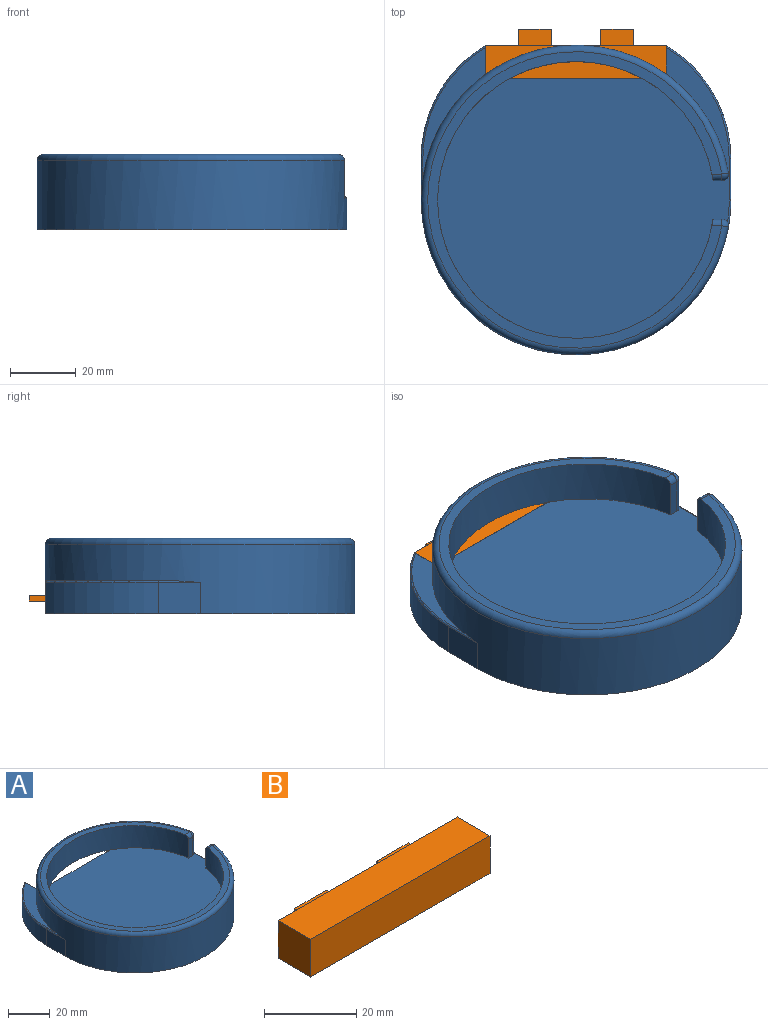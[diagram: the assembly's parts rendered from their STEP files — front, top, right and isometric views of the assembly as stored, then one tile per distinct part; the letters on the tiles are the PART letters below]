
ASSEMBLY  parts=2 mates=1
PART A: 30 faces, bbox 101.7x102.2x23.1 mm
  f0: cylinder r=42.17mm len=84.35mm, axis (0,0,-1), area 3289.9mm2, adj f5,f6,f8,f14,f15,f19,f22
  f1: plane 10x0.05mm, normal (1,0,0), area 0.5mm2, adj f4,f5,f10,f13
  f2: plane 39.64x19.18mm, normal (0,0,1), area 175.6mm2, adj f3,f9,f25,f26
  f3: cylinder r=47.18mm len=94.35mm, axis (0,0,-1), area 4558.3mm2, adj f2,f4,f5,f7,f8,f12,f16,f17
  f4: plane 94.35x94.25mm, normal (0,0,-1), area 6989.5mm2, adj f1,f3,f7,f9,f10,f11,f12,f13
  f5: plane 88.85x88.62mm, normal (0,0,1), area 5678.6mm2, adj f0,f1,f3,f10,f11,f13,f14,f15
  f6: plane 90.35x89.66mm, normal (0,0,1), area 775.7mm2, adj f0,f16,f19,f22
  f7: plane 12.62x9.5mm, normal (-1,0,0), area 119.9mm2, adj f3,f4,f24,f25
  f8: plane 55x10.15mm, normal (0,0,-1), area 261.9mm2, adj f0,f3,f9,f10,f11,f13
  f9: plane 10.12x10.12mm, normal (1,0,0), area 99.9mm2, adj f2,f4,f8,f10,f24,f26
  f10: plane 27.5x10mm, normal (0,1,0), area 275mm2, adj f1,f4,f5,f8,f9
  f11: plane 10.12x10.12mm, normal (-1,0,0), area 99.9mm2, adj f4,f5,f8,f13,f23,f29
  f12: plane 12.57x9.5mm, normal (1,0,0), area 119.4mm2, adj f3,f4,f23,f28
  f13: plane 27.5x10mm, normal (0,1,0), area 275mm2, adj f1,f4,f5,f8,f11
  f14: plane 11x2.72mm, normal (0,1,0), area 29.9mm2, adj f0,f5,f17,f19
  f15: plane 11x2.72mm, normal (0,-1,0), area 29.9mm2, adj f0,f5,f20,f22
  f16: torus R=45.17mm, axis (0,0,-1), area 865.7mm2, adj f3,f6,f18,f21
  f17: cylinder r=2mm len=11.5mm, axis (0,0,-1), area 38.8mm2, adj f3,f5,f14,f18,f27
  f18: sphere r=2mm, area 6.8mm2, adj f16,f17,f19
  f19: cylinder r=2mm len=3.05mm, axis (1,0,0), area 9.1mm2, adj f0,f6,f14,f18
  f20: cylinder r=2mm len=11mm, axis (0,0,-1), area 38.4mm2, adj f3,f5,f15,f21
  f21: sphere r=2mm, area 6.8mm2, adj f16,f20,f22
  f22: cylinder r=2mm len=3.05mm, axis (-1,0,0), area 9.1mm2, adj f0,f6,f15,f21
  f23: cylinder r=40mm len=34.45mm, axis (0,0,1), area 394.4mm2, adj f4,f11,f12,f29
  f24: cylinder r=40mm len=34.45mm, axis (0,0,1), area 394.4mm2, adj f4,f7,f9,f26
  f25: cylinder r=0.5mm len=12.62mm, axis (0,1,0), area 7.2mm2, adj f2,f3,f7,f26
  f26: torus R=39.5mm, axis (0,0,-1), area 32.3mm2, adj f2,f9,f24,f25
  f27: torus R=46.68mm, axis (0,0,-1), area 5.9mm2, adj f3,f5,f17,f28
  f28: cylinder r=0.5mm len=12.57mm, axis (0,-1,0), area 9.9mm2, adj f5,f12,f27,f29
  f29: torus R=39.5mm, axis (0,0,-1), area 32.3mm2, adj f5,f11,f23,f28
PART B: 16 faces, bbox 55x15x10 mm
  f0: plane 55x10mm, normal (0,0,1), area 550mm2, adj f1,f3,f4,f5
  f1: plane 10x10mm, normal (-1,0,0), area 100mm2, adj f0,f2,f4,f5
  f2: plane 55x10mm, normal (0,0,-1), area 550mm2, adj f1,f3,f4,f5
  f3: plane 10x10mm, normal (1,0,0), area 100mm2, adj f0,f2,f4,f5
  f4: plane 55x10mm, normal (0,-1,0), area 550mm2, adj f0,f1,f2,f3
  f5: plane 55x10mm, normal (0,1,0), area 514.7mm2, adj f0,f1,f2,f3,f6,f7,f8,f9
  f6: plane 5x1.8mm, normal (-1,0,0), area 9mm2, adj f5,f7,f9,f10
  f7: plane 9.8x5mm, normal (0,0,-1), area 49mm2, adj f5,f6,f8,f10
  f8: plane 5x1.8mm, normal (1,0,0), area 9mm2, adj f5,f7,f9,f10
  f9: plane 9.8x5mm, normal (0,0,1), area 49mm2, adj f5,f6,f8,f10
  f10: plane 9.8x1.8mm, normal (0,1,0), area 17.6mm2, adj f6,f7,f8,f9
  f11: plane 5x1.8mm, normal (-1,0,0), area 9mm2, adj f5,f12,f14,f15
  f12: plane 9.8x5mm, normal (0,0,-1), area 49mm2, adj f5,f11,f13,f15
  f13: plane 5x1.8mm, normal (1,0,0), area 9mm2, adj f5,f12,f14,f15
  f14: plane 9.8x5mm, normal (0,0,1), area 49mm2, adj f5,f11,f13,f15
  f15: plane 9.8x1.8mm, normal (0,1,0), area 17.6mm2, adj f11,f12,f13,f14
PLACE A t=(14.71,-84.99,-23.19)mm
PLACE B t=(14.78,-37.91,-71.27)mm
MATE parallel B.f4 <-> A.f10  axis (0,-1,0) through (14.71,-47.91,-28.19)mm
